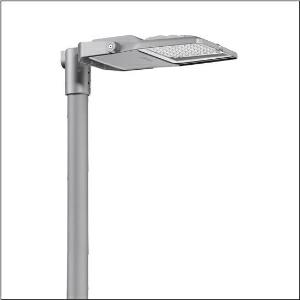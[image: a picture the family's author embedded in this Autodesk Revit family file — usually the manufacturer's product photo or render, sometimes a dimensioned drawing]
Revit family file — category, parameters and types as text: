
# Revit family: floodlight_fl_21_iq_mini___pl61_5xa7771d4c3a_f55b
name_source: partatom
category: Lighting Fixtures
units: mm (PartAtom-declared; Revit-internal decimal feet)

## family parameters
Cut with Voids When Loaded = No
Host = Face
Light Source = No
Part Type = Normal
Room Calculation Point = No
Round Connector Dimension = Use Diameter
Shared = No

## types (1)
- --- (1 x LED, 18260 lm, 143 W, 4000K)
    Apparent Load = 143 VA
    CIE Flux Codes = 33 65 98 100 100
    Color Rendering = 70
    Color Temperature = 4000K
    Default Elevation = 1800 mm
    Description = Floodlight FL 21 iQ mini, floodlight, primary light control with lens, of PMMA, primary optical cover: protective disc, of toughened safety glass, transparent, light distribution: PL61, light emission: direct distribution, installation type: surface-mounted, LED, High Power LED, rated luminous flux: 18.260lm, luminous efficacy: 128lm/W, light colour: 740, colour temperature: 4000K, control: Auto-Match, Temp-Guard, Lumen-Switch, Night-Set, Smart-Wire, Light-Fading, Desk-Remote (wireless, voltage-free reading and setting of iQ features in the workshop via application-optimized NFC function/RFID function), optimised constant luminous flux control (CLO 2.0), with terminal, 6-pole, mains connection: 220..240V, AC, 50/60Hz, start of lifetime: 143W, end of service life: 152W, reduction: 61W, luminaire housing, of diecast aluminium, powder-coated, Siteco® metallic grey (DB 702S), corrosivity category C5 mid according to DIN EN ISO 12944, sealing non-destructively replaceable, please order mast flange separately, mast bracket, of steel, galvanised, powder-coated, Siteco® metallic grey (DB 702S), protection rating (complete): IP66, insulation class (complete): insulation class II (safety insulation), certification: CE, ENEC, VDE, protection symbol: D, impact resistance: IK08, permissible operating ambient temperature: -40..+40°C, permissible operating ambient temperature for outdoor applications: -40..+50°C, standard: DIN EN 12944, LABS conformity tested according to VDMA 24364:2018-05, packaging unit: 1 piece

Light Distribution: PL61
    Height = 70 mm
    Lamp = 1 x LED
    Lamp Light Flux = 18260 lm
    Lamp Power = 143 W
    Lamp count = 1
    Length = 485 mm
    Luminous efficacy = 128 lm/W
    Manufacturer = Siteco
    ModVariant = No
    Model = 5XA7771D4C3A
    Number of Poles = 1
    OnlyDefault = Yes
    Power Factor = 1
    Product Name = Floodlight FL 21 iQ mini | PL61
    Product group = floodlight | pylon annexe
    ProductGroupID = 6200
    Protection Class = Protection class II
    Protection Degree = IP 66
    RLX_Detail_Level = 1
    RLX_Emergency_Light_Flux = 0 lm
    RLX_Emergency_Type = 0
    RLX_Emergency_Type_DB = No
    RlxData = <blob elided: 101749 chars, md5=5dfc84e9>
    Socket = socket
    Standby Power = 0 W
    System Light Flux = 18260 lm
    System Power = 143 W
    Type Comments = factory setting: luminous flux: 100 % | dim-lin: 254 | 730 mA
    Type Image = l_1007125.jpg
    URL = http://relux.com
    VarID = @adj_123531
    Voltage = 0 V
    Weight = 0.00 kg
    Width = 337 mm

## geometry (parser evidence)
native form markers: Blend x4, Sweep x12
no freeform markers — native parametric forms only
